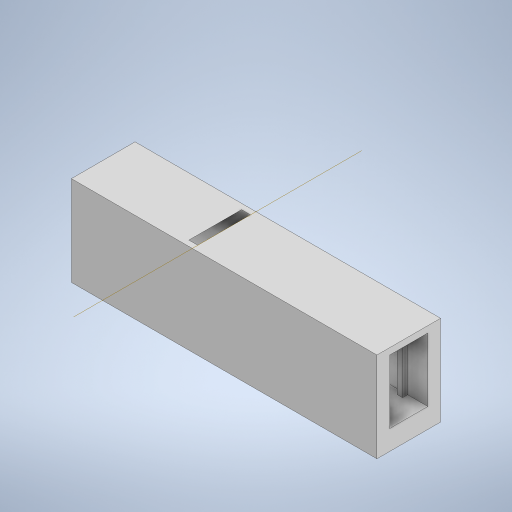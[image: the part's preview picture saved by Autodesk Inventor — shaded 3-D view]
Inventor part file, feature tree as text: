
AUTODESK INVENTOR PART (.ipt)
format: ipt  version: 2023 (Build 270158000, 158)  size: 412,672 bytes
history: native  units: in
note: dims shown in document units (in); Inventor stores cm internally (conversion verified against a paired STEP export)
features: extrude x7, sketch x7, plane x1
ambient origin geometry x8: Origin, YZ Plane, XZ Plane, XY Plane, X Axis, Y Axis, Z Axis, Center Point
bodies: Solid1 (feature_tree)
feature tree (15):
  extrude  "Extrusion1"  Depth=1.25in
  extrude  "Extrusion2"  Depth=0.55in
  extrude  "Extrusion3"  Depth=0.07in TaperAngle=0.0deg
  extrude  "Extrusion4"  TaperAngle=0.0deg  [1 undecoded]
  extrude  "Extrusion5"  Depth=0.0625in
  extrude  "Extrusion6"  Depth=0.25in
  plane  "Work Plane1"
  extrude  "Extrusion7"  Depth=0.1in
  sketch  "Sketch1"  dims[d0=6.0in d1=1.25in]
  sketch  "Sketch2"  dims[d2=1.2in d3=0.55in]
  sketch  "Sketch3"  dims[d4=1.0in d5=0.07in d6=0.0in]
  sketch  "Sketch4"  dims[d7=1.2in d8=0.0in]
  sketch  "Sketch5"  dims[d9=0.07in d10=0.0in d11=0.0625in]
  sketch  "Sketch6"  dims[d12=0.25in d13=0.0in d14=0.25in]
  sketch  "Sketch7"  dims[d15=0.1in d16=0.1in d17=0.1in d18=0.1in d19=0.1in d20=0.1in d21=1.0in d22=0.1in d23=0.1in d24=0.1in d25=0.1in d26=0.1in d27=0.1in d28=0.1in d29=0.1in d30=0.1in d31=0.1in d32=0.1in d33=0.1in d34=1.0in d35=1.0in d36=1.0in d37=1.25in d38=0.0in d39=0.1in d40=0.1in d41=0.1in d42=0.1in d43=0.1in d44=0.1in d45=1.0in d46=1.0in d47=0.1in d48=0.1in d49=1.0in d50=0.1in d51=0.1in d52=1.0in d53=1.25in d54=0.0in d55=0.125in d56=0.0in d57=45.0deg d58=0.0in d59=5.0in d60=0.125in d61=0.0in d62=0.5in d63=0.0344in]
note: 1 required parameter value undecoded (feature->parameter linkage not recoverable at this tier; creation-order binding heuristic only, values carry confidence <= 0.55)
